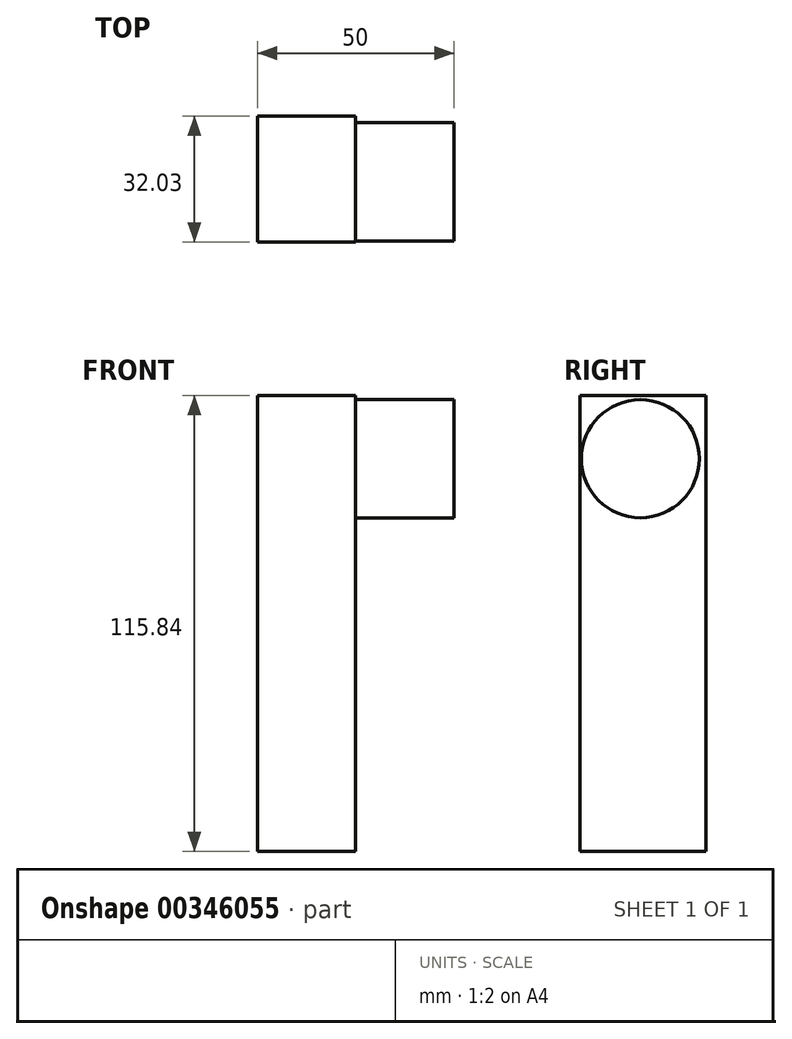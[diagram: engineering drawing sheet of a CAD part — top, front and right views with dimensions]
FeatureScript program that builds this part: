
annotation { "Feature Type Name" : "Feature", "Feature Type Description" : "" }
export const myFeature = defineFeature(function(context is Context, id is Id, definition is map)
    precondition{}
    {
        {
            var Q0;
            Q0=qCreatedBy(makeId("Right.planeOp"),FACE);
            var sketch = newSketch(context, id + "F0", { "sketchPlane" : qUnion([Q0])});
            skLineSegment(sketch, "E0", {"start": v(0, 0) * mm, "end": v(0, 115.84) * mm});
            skLineSegment(sketch, "E1", {"start": v(0, 115.84) * mm, "end": v(32.03, 115.84) * mm});
            skLineSegment(sketch, "E2", {"start": v(32.03, 115.84) * mm, "end": v(32.03, 0) * mm});
            skLineSegment(sketch, "E3", {"start": v(32.03, 0) * mm, "end": v(0, 0) * mm});
            skSolve(sketch);
        }
        {
            var Q0;
            Q0=makeQuery(id+"F0.imprint","IMPRINT",FACE,{"disambiguationData":[TD([[makeQuery(id+"F0.imprint","IMPRINT",EDGE,{"derivedFrom":sQuery(id+"F0.wireOp",EDGE,"E0")}),-1.0]])]});
            extrude(context, id + "F1", {"entities" : qUnion([Q0]), "depth" : 25 * mm});
        }
        {
            var Q0;
            Q0=makeQuery(id+"F1.opExtrude","CAP_FACE",FACE,{"disambiguationData":[OSD([sQuery(id+"F0.wireOp",EDGE,"E0"),sQuery(id+"F0.wireOp",EDGE,"E1"),sQuery(id+"F0.wireOp",EDGE,"E2"),sQuery(id+"F0.wireOp",EDGE,"E3")])],"isStart":false});
            var sketch = newSketch(context, id + "F2", { "sketchPlane" : qUnion([Q0])});
            skCircle(sketch, "E4", {"center": v(15.3, 99.8) * mm, "radius": 15 * mm});
            skSolve(sketch);
        }
        {
            var Q0;
            Q0=makeQuery(id+"F2.imprint","IMPRINT",FACE,{"disambiguationData":[TD([[makeQuery(id+"F2.imprint","IMPRINT",EDGE,{"derivedFrom":sQuery(id+"F2.wireOp",EDGE,"E4")}),1.0]])]});
            extrude(context, id + "F3", {"entities" : qUnion([Q0]), "operationType" : NewBodyOperationType.ADD, "depth" : 25 * mm});
        }
    });
